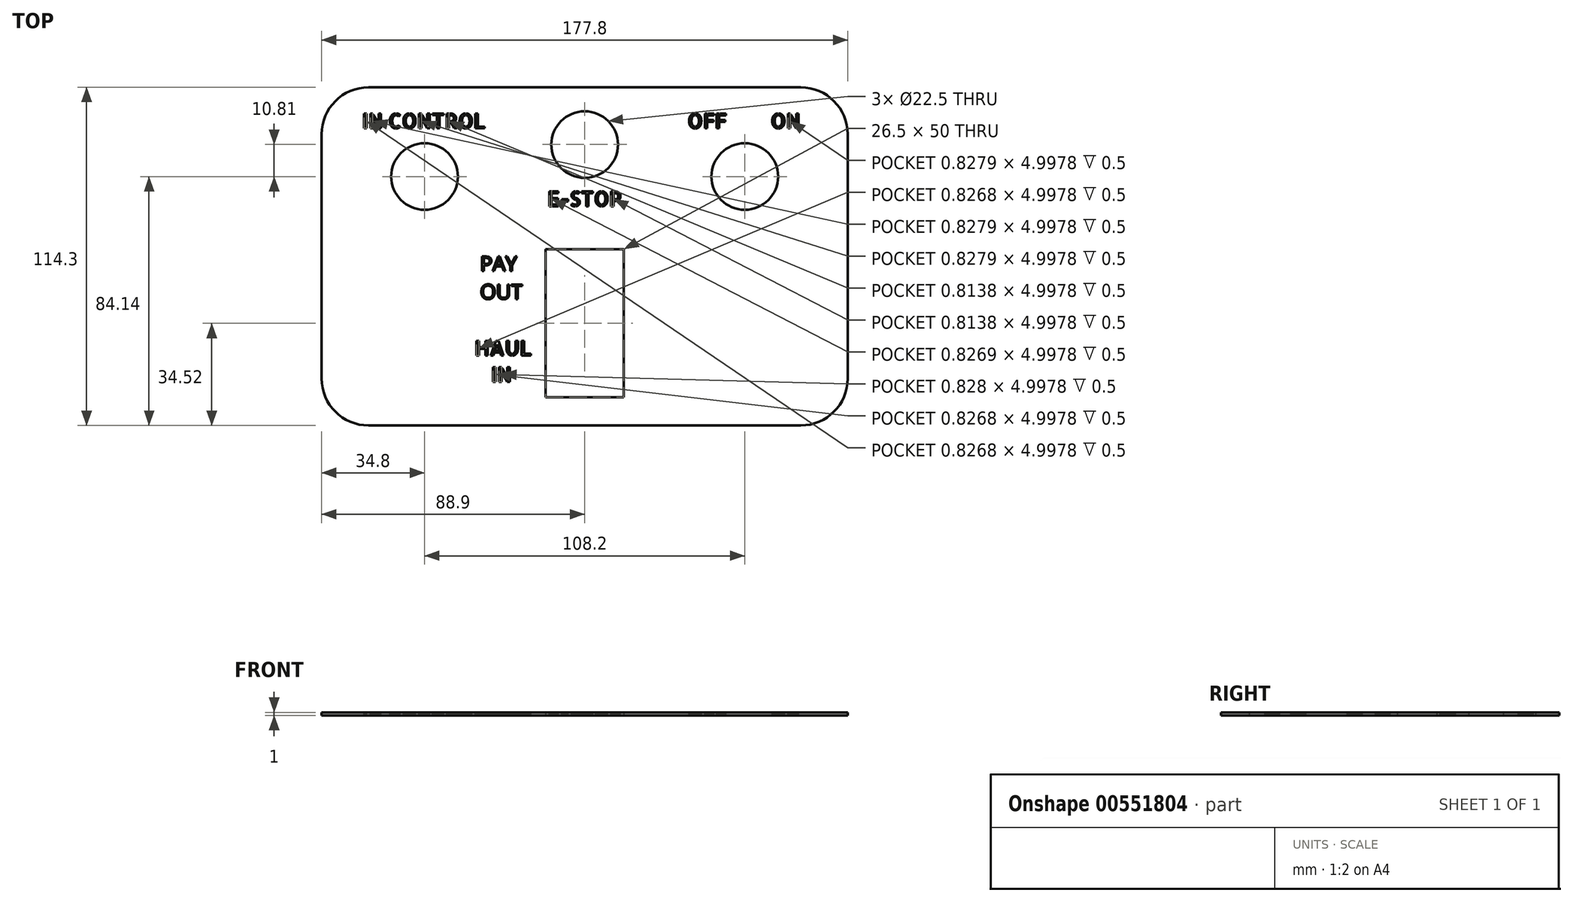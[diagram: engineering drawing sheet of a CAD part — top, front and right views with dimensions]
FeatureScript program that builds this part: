
annotation { "Feature Type Name" : "Feature", "Feature Type Description" : "" }
export const myFeature = defineFeature(function(context is Context, id is Id, definition is map)
    precondition{}
    {
        {
            var Q0;
            Q0=qCreatedBy(makeId("Top.planeOp"),FACE);
            var sketch = newSketch(context, id + "F0", { "sketchPlane" : qUnion([Q0])});
            skLineSegment(sketch, "E0.bottom", {"start": v(88.9, -57.15) * mm, "end": v(-88.9, -57.15) * mm});
            skLineSegment(sketch, "E0.top", {"start": v(88.9, 57.15) * mm, "end": v(-88.9, 57.15) * mm});
            skLineSegment(sketch, "E0.left", {"start": v(88.9, -57.15) * mm, "end": v(88.9, 57.15) * mm});
            skLineSegment(sketch, "E0.right", {"start": v(-88.9, -57.15) * mm, "end": v(-88.9, 57.15) * mm});
            skPoint(sketch, "E0.middle", {"position": v(0, 0) * mm});
            skCircle(sketch, "E1", {"center": v(-54.1, 26.99) * mm, "radius": 11.25 * mm});
            skCircle(sketch, "E2", {"center": v(54.1, 27) * mm, "radius": 11.25 * mm});
            skCircle(sketch, "E3", {"center": v(0, 37.8) * mm, "radius": 11.25 * mm});
            skLineSegment(sketch, "E4.bottom", {"start": v(13.25, -47.63) * mm, "end": v(-13.25, -47.63) * mm});
            skLineSegment(sketch, "E4.top", {"start": v(13.25, 2.37) * mm, "end": v(-13.25, 2.37) * mm});
            skLineSegment(sketch, "E4.left", {"start": v(13.25, -47.63) * mm, "end": v(13.25, 2.37) * mm});
            skLineSegment(sketch, "E4.right", {"start": v(-13.25, -47.63) * mm, "end": v(-13.25, 2.37) * mm});
            skPoint(sketch, "E4.middle", {"position": v(0, -22.63) * mm});
            skSolve(sketch);
        }
        {
            var Q0;
            Q0 = qSketchRegion(id + "F0", true);
            extrude(context, id + "F1", {"entities" : qUnion([Q0]), "depth" : 1 * mm, "offsetDistance" : 25 * mm});
        }
        {
            var Q0;
            Q0=makeQuery(id+"F1.opExtrude","SWEPT_EDGE",EDGE,{"disambiguationData":[OSD([sQuery(id+"F0.wireOp",EDGE,"E0.top"),sQuery(id+"F0.wireOp",EDGE,"E0.right")])]});
            var Q1;
            Q1=makeQuery(id+"F1.opExtrude","SWEPT_EDGE",EDGE,{"disambiguationData":[OSD([sQuery(id+"F0.wireOp",EDGE,"E0.top"),sQuery(id+"F0.wireOp",EDGE,"E0.left")])]});
            var Q2;
            Q2=makeQuery(id+"F1.opExtrude","SWEPT_EDGE",EDGE,{"disambiguationData":[OSD([sQuery(id+"F0.wireOp",EDGE,"E0.bottom"),sQuery(id+"F0.wireOp",EDGE,"E0.left")])]});
            var Q3;
            Q3=makeQuery(id+"F1.opExtrude","SWEPT_EDGE",EDGE,{"disambiguationData":[OSD([sQuery(id+"F0.wireOp",EDGE,"E0.bottom"),sQuery(id+"F0.wireOp",EDGE,"E0.right")])]});
            fillet(context, id + "F2", {"entities" : qUnion([Q0, Q1, Q2, Q3]), "radius" : 15.88 * mm, "tangentPropagation" : true, "allowEdgeOverflow" : false});
        }
        {
            var Q0;
            Q0=makeQuery(id+"F1.opExtrude","CAP_FACE",FACE,{"disambiguationData":[OSD([sQuery(id+"F0.wireOp",EDGE,"E0.bottom"),sQuery(id+"F0.wireOp",EDGE,"E0.top"),sQuery(id+"F0.wireOp",EDGE,"E0.left"),sQuery(id+"F0.wireOp",EDGE,"E0.right"),sQuery(id+"F0.wireOp",EDGE,"E1"),sQuery(id+"F0.wireOp",EDGE,"E2"),sQuery(id+"F0.wireOp",EDGE,"E3"),sQuery(id+"F0.wireOp",EDGE,"E4.bottom"),sQuery(id+"F0.wireOp",EDGE,"E4.top"),sQuery(id+"F0.wireOp",EDGE,"E4.left"),sQuery(id+"F0.wireOp",EDGE,"E4.right")])],"isStart":false});
            var sketch = newSketch(context, id + "F3", { "sketchPlane" : qUnion([Q0])});
            skText(sketch, "E5", { "text": "IN CONTROL", "fontName": "AllertaStencil-Regular.ttf"});
            skText(sketch, "E6", { "text": "OFF        ON", "fontName": "AllertaStencil-Regular.ttf"});
            skText(sketch, "E7", { "text": "PAY\nOUT", "fontName": "OpenSans-Regular.ttf"});
            skText(sketch, "E8", { "text": "HAUL\n   IN", "fontName": "AllertaStencil-Regular.ttf"});
            skText(sketch, "E9", { "text": "E-STOP", "fontName": "AllertaStencil-Regular.ttf"});
            const initialGuessF3  = {"E5": [-0.07515, 0.04326, 1, 0, 0.005], "E6": [0.03475, 0.04326, 1, 0, 0.005], "E7": [-0.03533, -0.005, 1, 0, 0.005], "E8": [-0.03719, -0.0335, 1, 0, 0.005], "E9": [-0.01263, 0.01693, 1, 0, 0.005]};
            skSetInitialGuess(sketch, initialGuessF3);
            skSolve(sketch);
        }
        {
            var Q0;
            Q0 = qSketchRegion(id + "F3", true);
            extrude(context, id + "F4", {"entities" : qUnion([Q0]), "operationType" : NewBodyOperationType.REMOVE, "oppositeDirection" : true, "depth" : 0.5 * mm, "offsetDistance" : 25 * mm});
        }
    });
